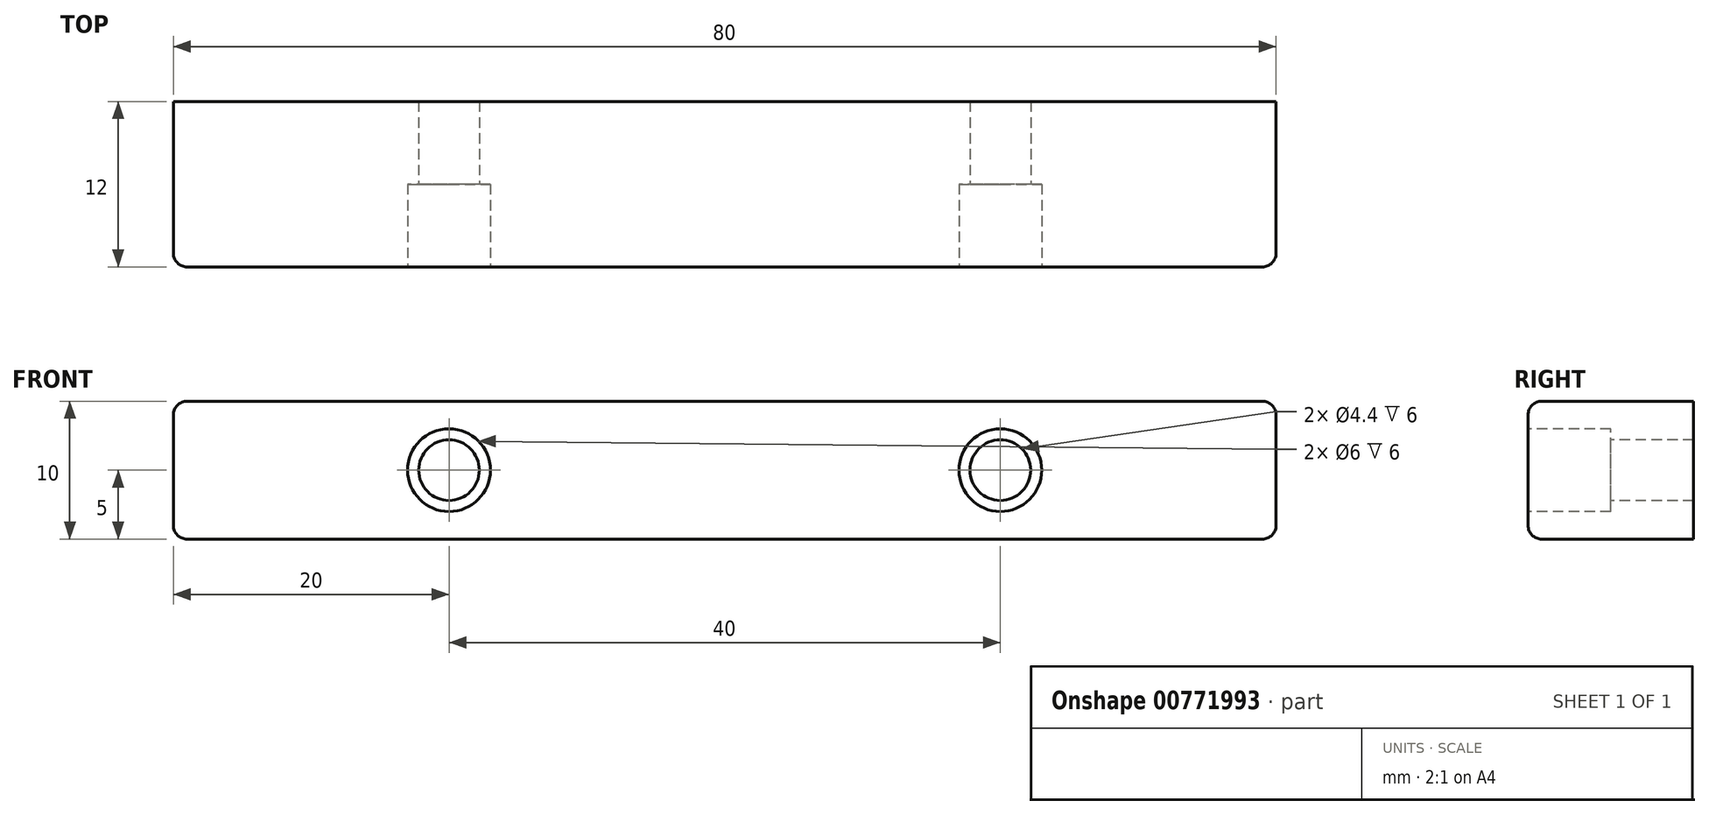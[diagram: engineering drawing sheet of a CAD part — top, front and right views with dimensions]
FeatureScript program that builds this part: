
annotation { "Feature Type Name" : "Feature", "Feature Type Description" : "" }
export const myFeature = defineFeature(function(context is Context, id is Id, definition is map)
    precondition{}
    {
        {
            var Q0;
            Q0=qCreatedBy(makeId("Top.planeOp"),FACE);
            var sketch = newSketch(context, id + "F0", { "sketchPlane" : qUnion([Q0])});
            skLineSegment(sketch, "E0.bottom", {"start": v(40, -6) * mm, "end": v(-40, -6) * mm});
            skLineSegment(sketch, "E0.top", {"start": v(40, 6) * mm, "end": v(-40, 6) * mm});
            skLineSegment(sketch, "E0.left", {"start": v(40, -6) * mm, "end": v(40, 6) * mm});
            skLineSegment(sketch, "E0.right", {"start": v(-40, -6) * mm, "end": v(-40, 6) * mm});
            skPoint(sketch, "E0.middle", {"position": v(0, 0) * mm});
            skSolve(sketch);
        }
        {
            var Q0;
            Q0=makeQuery(id+"F0.imprint","IMPRINT",FACE,{"disambiguationData":[TD([[makeQuery(id+"F0.imprint","IMPRINT",EDGE,{"derivedFrom":sQuery(id+"F0.wireOp",EDGE,"E0.bottom")}),-1.0]])]});
            extrude(context, id + "F1", {"entities" : qUnion([Q0]), "depth" : 10 * mm, "offsetDistance" : 25 * mm});
        }
        {
            var Q0;
            Q0=makeQuery(id+"F1.opExtrude","SWEPT_FACE",FACE,{"disambiguationData":[OSD([sQuery(id+"F0.wireOp",EDGE,"E0.bottom")])]});
            var sketch = newSketch(context, id + "F2", { "sketchPlane" : qUnion([Q0])});
            skCircle(sketch, "E1", {"center": v(-20, 5) * mm, "radius": 2.2 * mm});
            skCircle(sketch, "E2", {"center": v(-20, 5) * mm, "radius": 3 * mm});
            skCircle(sketch, "E3", {"center": v(20, 5) * mm, "radius": 2.2 * mm});
            skCircle(sketch, "E4", {"center": v(20, 5) * mm, "radius": 3 * mm});
            skSolve(sketch);
        }
        {
            var Q0;
            Q0=makeQuery(id+"F2.imprint","IMPRINT",FACE,{"disambiguationData":[TD([[makeQuery(id+"F2.imprint","IMPRINT",EDGE,{"derivedFrom":sQuery(id+"F2.wireOp",EDGE,"E1")}),1.0]])]});
            var Q1;
            Q1=makeQuery(id+"F2.imprint","IMPRINT",FACE,{"disambiguationData":[TD([[makeQuery(id+"F2.imprint","IMPRINT",EDGE,{"derivedFrom":sQuery(id+"F2.wireOp",EDGE,"E3")}),1.0]])]});
            var Q2;
            Q2=sQuery(id+"F2.wireOp",EDGE,"E1");
            extrude(context, id + "F3", {"entities" : qUnion([Q0, Q1]), "operationType" : NewBodyOperationType.REMOVE, "surfaceEntities" : qUnion([Q2]), "endBound" : BoundingType.THROUGH_ALL, "oppositeDirection" : true, "depth" : 25 * mm, "offsetDistance" : 25 * mm});
        }
        {
            var Q0;
            Q0=makeQuery(id+"F2.imprint","IMPRINT",FACE,{"disambiguationData":[TD([[makeQuery(id+"F2.imprint","IMPRINT",EDGE,{"derivedFrom":sQuery(id+"F2.wireOp",EDGE,"E1")}),-1.0]])]});
            var Q1;
            Q1=makeQuery(id+"F2.imprint","IMPRINT",FACE,{"disambiguationData":[TD([[makeQuery(id+"F2.imprint","IMPRINT",EDGE,{"derivedFrom":sQuery(id+"F2.wireOp",EDGE,"E3")}),-1.0]])]});
            extrude(context, id + "F4", {"entities" : qUnion([Q0, Q1]), "operationType" : NewBodyOperationType.REMOVE, "oppositeDirection" : true, "depth" : 6 * mm, "offsetDistance" : 25 * mm});
        }
        {
            var Q0;
            Q0=makeQuery(id+"F1.opExtrude","CAP_EDGE",EDGE,{"disambiguationData":[OSD([sQuery(id+"F0.wireOp",EDGE,"E0.bottom")])],"isStart":false});
            var Q1;
            Q1=makeQuery(id+"F1.opExtrude","CAP_EDGE",EDGE,{"disambiguationData":[OSD([sQuery(id+"F0.wireOp",EDGE,"E0.right")])],"isStart":false});
            var Q2;
            Q2=makeQuery(id+"F1.opExtrude","CAP_EDGE",EDGE,{"disambiguationData":[OSD([sQuery(id+"F0.wireOp",EDGE,"E0.left")])],"isStart":false});
            var Q3;
            Q3=makeQuery(id+"F1.opExtrude","CAP_EDGE",EDGE,{"disambiguationData":[OSD([sQuery(id+"F0.wireOp",EDGE,"E0.right")])],"isStart":true});
            var Q4;
            Q4=makeQuery(id+"F1.opExtrude","CAP_EDGE",EDGE,{"disambiguationData":[OSD([sQuery(id+"F0.wireOp",EDGE,"E0.bottom")])],"isStart":true});
            var Q5;
            Q5=makeQuery(id+"F1.opExtrude","SWEPT_EDGE",EDGE,{"disambiguationData":[OSD([sQuery(id+"F0.wireOp",EDGE,"E0.bottom"),sQuery(id+"F0.wireOp",EDGE,"E0.left")])]});
            var Q6;
            Q6=makeQuery(id+"F1.opExtrude","SWEPT_EDGE",EDGE,{"disambiguationData":[OSD([sQuery(id+"F0.wireOp",EDGE,"E0.bottom"),sQuery(id+"F0.wireOp",EDGE,"E0.right")])]});
            var Q7;
            Q7=makeQuery(id+"F1.opExtrude","CAP_EDGE",EDGE,{"disambiguationData":[OSD([sQuery(id+"F0.wireOp",EDGE,"E0.left")])],"isStart":true});
            fillet(context, id + "F5", {"entities" : qUnion([Q0, Q1, Q2, Q3, Q4, Q5, Q6, Q7]), "radius" : 1 * mm, "tangentPropagation" : true, "allowEdgeOverflow" : false});
        }
    });
